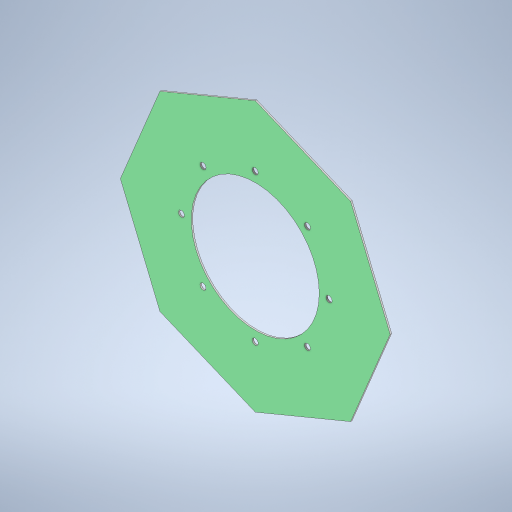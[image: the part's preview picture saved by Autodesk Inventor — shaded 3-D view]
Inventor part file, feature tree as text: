
AUTODESK INVENTOR PART (.ipt)
format: ipt  version: 2024.2 (Build 282272000, 272)  size: 296,960 bytes
history: native  units: mm
features: sketch x2, other x2, sheet_metal_op x1, extrude x1, pattern_circular x1
ambient origin geometry x8: Origin, YZ Plane, XZ Plane, XY Plane, X Axis, Y Axis, Z Axis, Center Point
bodies: Solid1 (feature_tree)
feature tree (7):
  sheet_metal_op  "Face1"
  extrude  "Extrusion1"  Depth=150.0mm
  pattern_circular  "Circular Pattern1"  Count=15  [1 undecoded]
  sketch  "Sketch2"  dims[d15=3.0mm d16=12.5mm d17=150.0mm]
  other  "Plate1"
  sketch  "Sketch4"  dims[d18=10.0mm d19=0.0mm d20=80.0mm d21=360.0deg d23=506.0mm d26=260.0mm]
  other  "Definition1"
note: 1 required parameter value undecoded (feature->parameter linkage not recoverable at this tier; creation-order binding heuristic only, values carry confidence <= 0.55)
